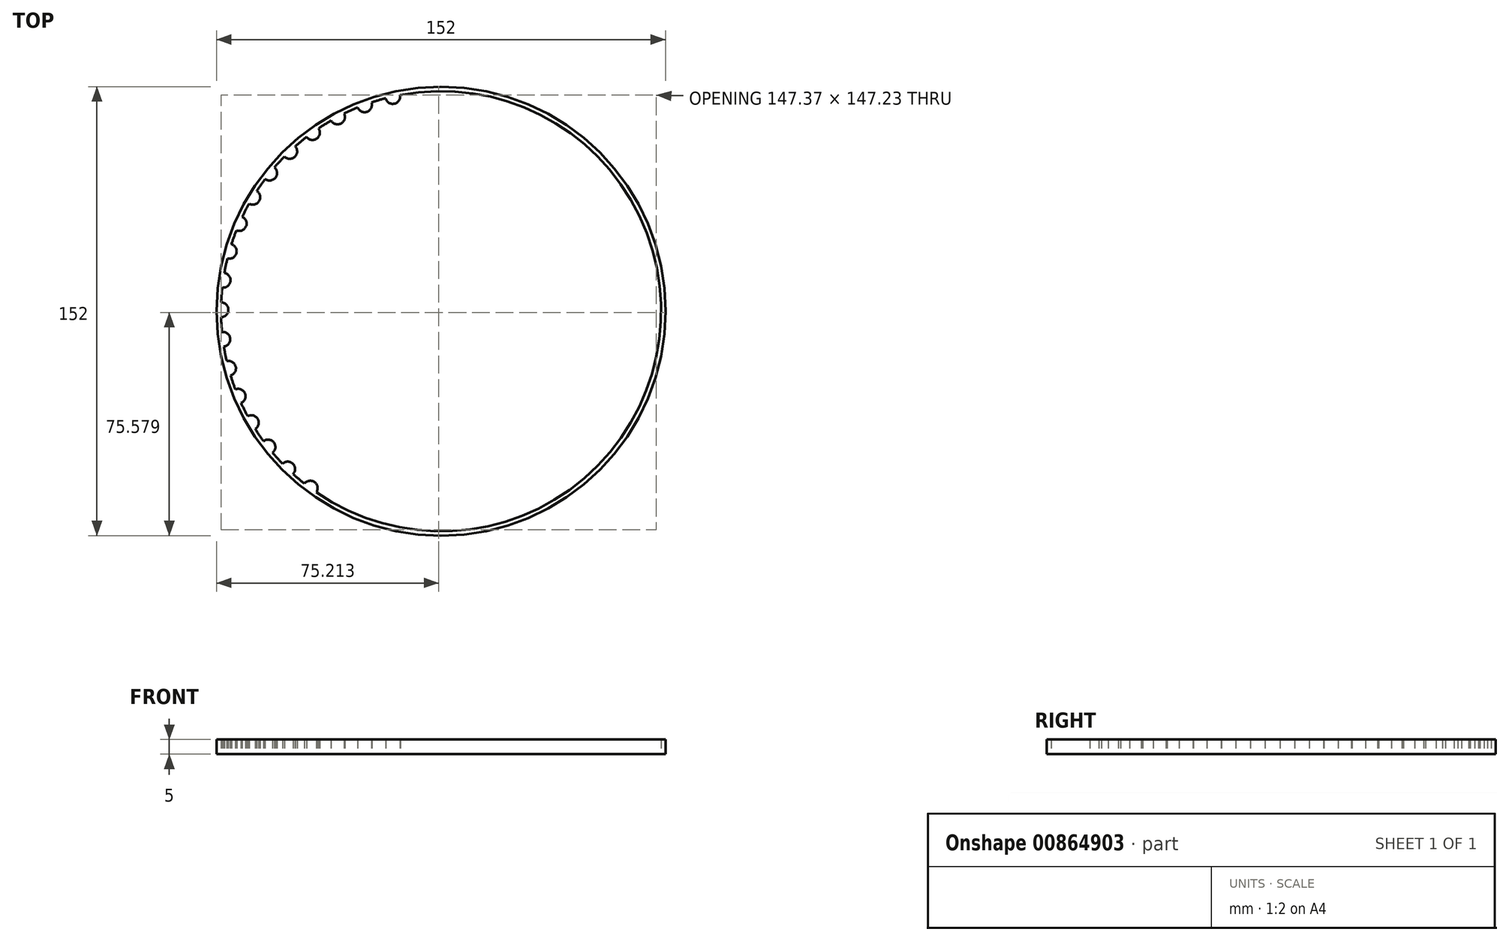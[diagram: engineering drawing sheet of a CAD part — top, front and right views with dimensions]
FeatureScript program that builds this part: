
annotation { "Feature Type Name" : "Feature", "Feature Type Description" : "" }
export const myFeature = defineFeature(function(context is Context, id is Id, definition is map)
    precondition{}
    {
        {
            var Q0;
            Q0=qCreatedBy(makeId("Top.planeOp"),FACE);
            var sketch = newSketch(context, id + "F0", { "sketchPlane" : qUnion([Q0])});
            skCircle(sketch, "E0", {"center": v(0, 0) * mm, "radius": 76 * mm});
            skArc(sketch, "E1", {"start": v(-59.55, 44.77) * mm, "mid": v(-61.02, 42.75) * mm, "end": v(-62.42, 40.67) * mm});
            skArc(sketch, "E2", {"start": v(-65, 36.4) * mm, "mid": v(-61.6, 37.26) * mm, "end": v(-62.42, 40.67) * mm});
            skArc(sketch, "E3", {"start": v(-59.55, 44.77) * mm, "mid": v(-56.06, 45.18) * mm, "end": v(-56.4, 48.66) * mm});
            skArc(sketch, "E4.trimOffspring", {"start": v(-65, 36.4) * mm, "mid": v(-66.2, 34.19) * mm, "end": v(-67.3, 31.95) * mm});
            skArc(sketch, "E5", {"start": v(-53.01, 52.34) * mm, "mid": v(-49.5, 52.28) * mm, "end": v(-49.38, 55.78) * mm});
            skArc(sketch, "E6", {"start": v(-45.53, 58.97) * mm, "mid": v(-42.06, 58.44) * mm, "end": v(-41.47, 61.9) * mm});
            skArc(sketch, "E7", {"start": v(-37.22, 64.54) * mm, "mid": v(-33.86, 63.54) * mm, "end": v(-32.8, 66.89) * mm});
            skArc(sketch, "E8", {"start": v(-28.24, 68.94) * mm, "mid": v(-25.04, 67.5) * mm, "end": v(-23.55, 70.68) * mm});
            skArc(sketch, "E9", {"start": v(-18.75, 72.1) * mm, "mid": v(-15.78, 70.25) * mm, "end": v(-13.87, 73.2) * mm});
            skArc(sketch, "E10", {"start": v(-69.3, 27.36) * mm, "mid": v(-66.04, 28.67) * mm, "end": v(-67.3, 31.95) * mm});
            skArc(sketch, "E11.trimOffspring", {"start": v(-53.01, 52.34) * mm, "mid": v(-54.74, 50.53) * mm, "end": v(-56.4, 48.66) * mm});
            skArc(sketch, "E12.trimOffspring", {"start": v(-45.53, 58.97) * mm, "mid": v(-47.48, 57.4) * mm, "end": v(-49.38, 55.78) * mm});
            skArc(sketch, "E13.trimOffspring", {"start": v(-37.22, 64.54) * mm, "mid": v(-39.37, 63.25) * mm, "end": v(-41.47, 61.9) * mm});
            skArc(sketch, "E14.trimOffspring", {"start": v(-28.24, 68.94) * mm, "mid": v(-30.54, 67.95) * mm, "end": v(-32.8, 66.89) * mm});
            skArc(sketch, "E15.trimOffspring", {"start": v(-18.75, 72.1) * mm, "mid": v(-21.16, 71.43) * mm, "end": v(-23.55, 70.68) * mm});
            skArc(sketch, "E16.trimOffspring", {"start": v(-69.3, 27.36) * mm, "mid": v(-70.17, 25.02) * mm, "end": v(-70.98, 22.64) * mm});
            skArc(sketch, "E17.trimOffspring", {"start": v(-72.33, 17.83) * mm, "mid": v(-69.29, 19.57) * mm, "end": v(-70.98, 22.64) * mm});
            skArc(sketch, "E18.trimOffspring", {"start": v(-72.33, 17.83) * mm, "mid": v(-72.9, 15.4) * mm, "end": v(-73.37, 12.93) * mm});
            skArc(sketch, "E19", {"start": v(-74.07, 7.98) * mm, "mid": v(-71.29, 10.11) * mm, "end": v(-73.37, 12.93) * mm});
            skArc(sketch, "E20", {"start": v(-74.47, -2.03) * mm, "mid": v(-72, 0.45) * mm, "end": v(-74.44, 2.96) * mm});
            skArc(sketch, "E21", {"start": v(-73.53, -12) * mm, "mid": v(-71.4, -9.21) * mm, "end": v(-74.17, -7.05) * mm});
            skArc(sketch, "E22", {"start": v(-71.26, -21.75) * mm, "mid": v(-69.53, -18.7) * mm, "end": v(-72.55, -16.92) * mm});
            skArc(sketch, "E23", {"start": v(-67.7, -31.1) * mm, "mid": v(-66.4, -27.84) * mm, "end": v(-69.63, -26.48) * mm});
            skArc(sketch, "E24", {"start": v(-62.93, -39.88) * mm, "mid": v(-62.07, -36.48) * mm, "end": v(-65.46, -35.57) * mm});
            skArc(sketch, "E25.trimOffspring", {"start": v(-74.07, 7.98) * mm, "mid": v(-74.3, 5.48) * mm, "end": v(-74.44, 2.96) * mm});
            skArc(sketch, "E26.trimOffspring", {"start": v(-74.47, -2.03) * mm, "mid": v(-74.36, -4.54) * mm, "end": v(-74.17, -7.05) * mm});
            skArc(sketch, "E27.trimOffspring", {"start": v(-73.53, -12) * mm, "mid": v(-73.08, -14.47) * mm, "end": v(-72.55, -16.92) * mm});
            skArc(sketch, "E28.trimOffspring", {"start": v(-71.26, -21.75) * mm, "mid": v(-70.48, -24.13) * mm, "end": v(-69.63, -26.48) * mm});
            skArc(sketch, "E29.trimOffspring", {"start": v(-67.7, -31.1) * mm, "mid": v(-66.62, -33.35) * mm, "end": v(-65.46, -35.57) * mm});
            skArc(sketch, "E30.trimOffspring", {"start": v(-62.93, -39.88) * mm, "mid": v(-61.55, -41.97) * mm, "end": v(-60.1, -44.02) * mm});
            skArc(sketch, "E31", {"start": v(-57.02, -47.95) * mm, "mid": v(-56.63, -44.46) * mm, "end": v(-60.1, -44.02) * mm});
            skArc(sketch, "E32", {"start": v(-50.08, -55.15) * mm, "mid": v(-50.16, -51.65) * mm, "end": v(-53.67, -51.67) * mm});
            skArc(sketch, "E33.trimOffspring", {"start": v(-57.02, -47.95) * mm, "mid": v(-55.38, -49.84) * mm, "end": v(-53.67, -51.67) * mm});
            skArc(sketch, "E34.trimOffspring", {"start": v(-50.08, -55.15) * mm, "mid": v(-48.2, -56.8) * mm, "end": v(-46.27, -58.4) * mm});
            skArc(sketch, "E35.trimOffspring", {"start": v(-42.25, -61.36) * mm, "mid": v(72.9, -15.37) * mm, "end": v(-13.87, 73.2) * mm});
            skPoint(sketch, "E36.center.orphan", {"position": v(-44.28, -59.91) * mm});
            skArc(sketch, "E37", {"start": v(-42.25, -61.36) * mm, "mid": v(-42.8, -57.9) * mm, "end": v(-46.27, -58.4) * mm});
            skSolve(sketch);
        }
        {
            var Q0;
            Q0=makeQuery(id+"F0.imprint","IMPRINT",FACE,{"disambiguationData":[TD([[makeQuery(id+"F0.imprint","IMPRINT",EDGE,{"derivedFrom":sQuery(id+"F0.wireOp",EDGE,"E0")}),1.0]])]});
            extrude(context, id + "F1", {"entities" : qUnion([Q0]), "depth" : 5 * mm, "offsetDistance" : 25 * mm});
        }
    });
